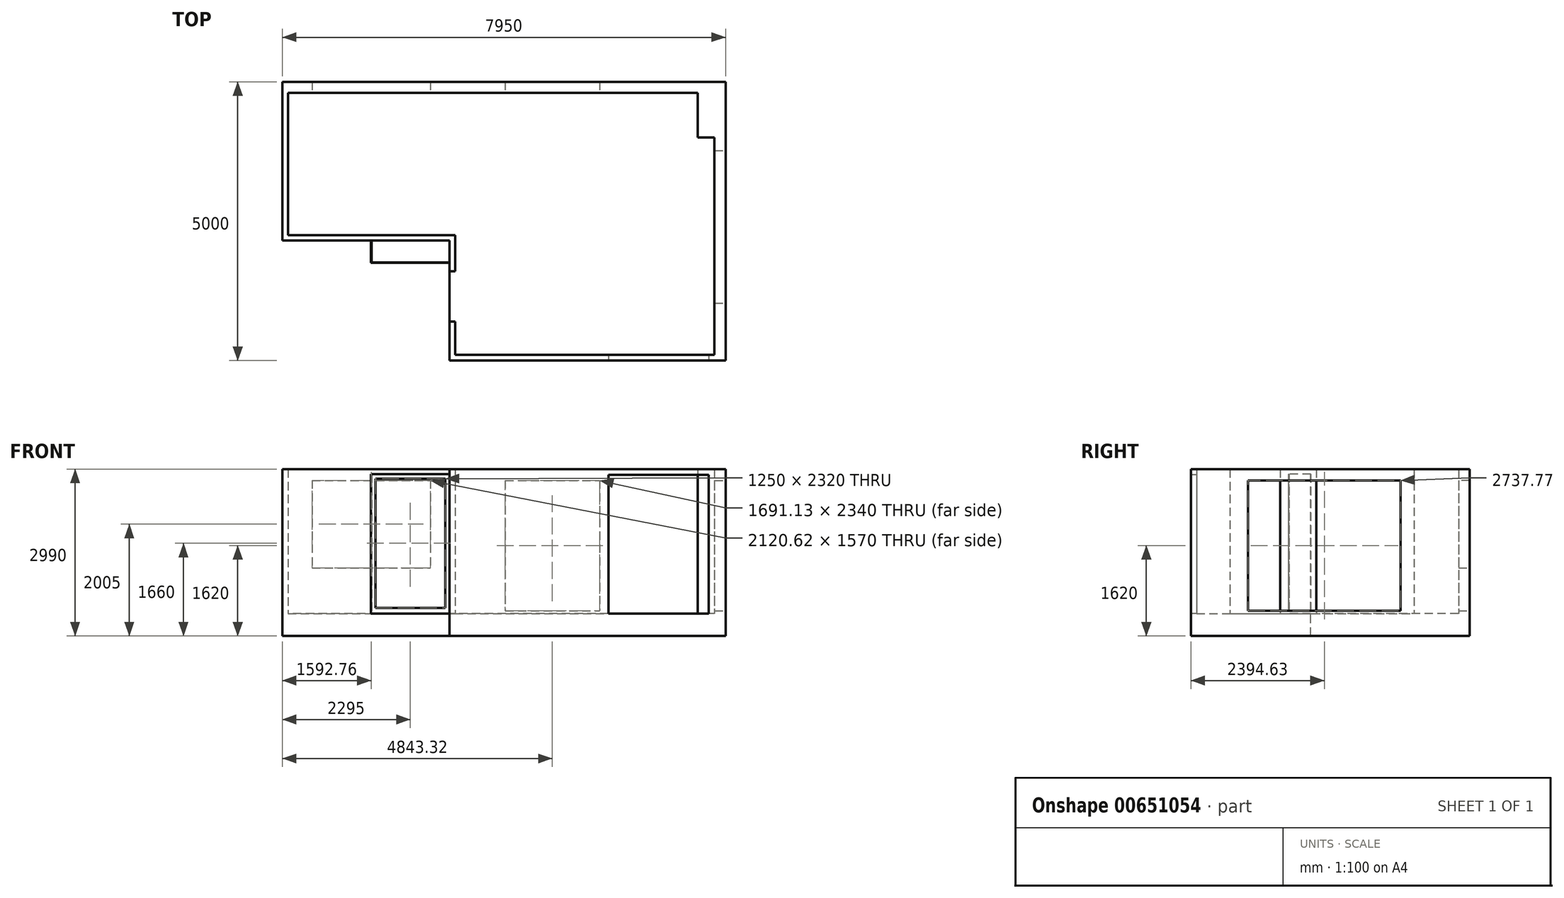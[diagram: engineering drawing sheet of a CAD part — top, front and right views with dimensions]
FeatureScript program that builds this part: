
annotation { "Feature Type Name" : "Feature", "Feature Type Description" : "" }
export const myFeature = defineFeature(function(context is Context, id is Id, definition is map)
    precondition{}
    {
        {
            var Q0;
            Q0=qCreatedBy(makeId("Top.planeOp"),FACE);
            var sketch = newSketch(context, id + "F0", { "sketchPlane" : qUnion([Q0])});
            skLineSegment(sketch, "E0.bottom", {"start": v(0, 0) * mm, "end": v(-4650, 0) * mm});
            skLineSegment(sketch, "E0.left", {"start": v(0, 0) * mm, "end": v(0, 3900) * mm});
            skLineSegment(sketch, "E0.right", {"start": v(-4650, 0) * mm, "end": v(-4650, 2150) * mm});
            skLineSegment(sketch, "E1.top", {"start": v(-4650, 2150) * mm, "end": v(-7650, 2150) * mm});
            skLineSegment(sketch, "E1.right", {"start": v(-7650, 4700) * mm, "end": v(-7650, 2150) * mm});
            skLineSegment(sketch, "E2", {"start": v(-7650, 4700) * mm, "end": v(-300, 4700) * mm});
            skLineSegment(sketch, "E3.bottom", {"start": v(-7750, 4900) * mm, "end": v(200, 4900) * mm});
            skLineSegment(sketch, "E3.top", {"start": v(-4750, -100) * mm, "end": v(200, -100) * mm});
            skLineSegment(sketch, "E3.left", {"start": v(-7750, 4900) * mm, "end": v(-7750, 2050) * mm});
            skLineSegment(sketch, "E3.right", {"start": v(200, 4900) * mm, "end": v(200, -100) * mm});
            skLineSegment(sketch, "E4.top", {"start": v(-7750, 2050) * mm, "end": v(-4750, 2050) * mm});
            skLineSegment(sketch, "E4.right", {"start": v(-4750, -100) * mm, "end": v(-4750, 2050) * mm});
            skLineSegment(sketch, "E5.bottom", {"start": v(-1900, 0) * mm, "end": v(-100, 0) * mm});
            skLineSegment(sketch, "E5.top", {"start": v(-1900, -100) * mm, "end": v(-100, -100) * mm});
            skLineSegment(sketch, "E5.left", {"start": v(-1900, 0) * mm, "end": v(-1900, -100) * mm});
            skLineSegment(sketch, "E5.right", {"start": v(-100, 0) * mm, "end": v(-100, -100) * mm});
            skLineSegment(sketch, "E6.bottom", {"start": v(-4750, 1500) * mm, "end": v(-4650, 1500) * mm});
            skLineSegment(sketch, "E6.top", {"start": v(-4750, 600) * mm, "end": v(-4650, 600) * mm});
            skLineSegment(sketch, "E6.left", {"start": v(-4750, 1500) * mm, "end": v(-4750, 600) * mm});
            skLineSegment(sketch, "E6.right", {"start": v(-4650, 1500) * mm, "end": v(-4650, 600) * mm});
            skLineSegment(sketch, "E7.bottom", {"start": v(-6160, 2050) * mm, "end": v(-4750, 2050) * mm});
            skLineSegment(sketch, "E7.top", {"start": v(-6160, 1650) * mm, "end": v(-4750, 1650) * mm});
            skLineSegment(sketch, "E7.left", {"start": v(-6160, 2050) * mm, "end": v(-6160, 1650) * mm});
            skLineSegment(sketch, "E7.right", {"start": v(-4750, 2050) * mm, "end": v(-4750, 1650) * mm});
            skLineSegment(sketch, "E8.bottom", {"start": v(-6150, 2050) * mm, "end": v(-4750, 2050) * mm});
            skLineSegment(sketch, "E8.top", {"start": v(-6150, 1660) * mm, "end": v(-4750, 1660) * mm});
            skLineSegment(sketch, "E8.left", {"start": v(-6150, 2050) * mm, "end": v(-6150, 1660) * mm});
            skLineSegment(sketch, "E8.right", {"start": v(-4750, 2050) * mm, "end": v(-4750, 1660) * mm});
            skLineSegment(sketch, "E9.top", {"start": v(-300, 3900) * mm, "end": v(0, 3900) * mm});
            skLineSegment(sketch, "E9.left", {"start": v(-300, 4700) * mm, "end": v(-300, 3900) * mm});
            skPoint(sketch, "E10.orphan", {"position": v(0, 4700) * mm});
            skLineSegment(sketch, "E11.bottom", {"start": v(0, 3663.51) * mm, "end": v(200, 3663.51) * mm});
            skLineSegment(sketch, "E11.top", {"start": v(0, 925.75) * mm, "end": v(200, 925.75) * mm});
            skLineSegment(sketch, "E11.left", {"start": v(0, 3663.51) * mm, "end": v(0, 925.75) * mm});
            skLineSegment(sketch, "E11.right", {"start": v(200, 3663.51) * mm, "end": v(200, 925.75) * mm});
            skLineSegment(sketch, "E12.bottom", {"start": v(-3752.24, 4700) * mm, "end": v(-2061.12, 4700) * mm});
            skLineSegment(sketch, "E12.top", {"start": v(-3752.24, 4900) * mm, "end": v(-2061.12, 4900) * mm});
            skLineSegment(sketch, "E12.left", {"start": v(-3752.24, 4700) * mm, "end": v(-3752.24, 4900) * mm});
            skLineSegment(sketch, "E12.right", {"start": v(-2061.12, 4700) * mm, "end": v(-2061.12, 4900) * mm});
            skLineSegment(sketch, "E13.bottom", {"start": v(-7217.55, 4700) * mm, "end": v(-5096.93, 4700) * mm});
            skLineSegment(sketch, "E13.top", {"start": v(-7217.55, 4900) * mm, "end": v(-5096.93, 4900) * mm});
            skLineSegment(sketch, "E13.left", {"start": v(-7217.55, 4700) * mm, "end": v(-7217.55, 4900) * mm});
            skLineSegment(sketch, "E13.right", {"start": v(-5096.93, 4700) * mm, "end": v(-5096.93, 4900) * mm});
            skSolve(sketch);
        }
        {
            var Q0;
            {var subQ7=sQuery(id+"F0.wireOp",EDGE,"E1.top");Q0=makeQuery(id+"F0.imprint","IMPRINT",FACE,{"disambiguationData":[TD([[makeQuery(id+"F0.imprint","IMPRINT",EDGE,{"derivedFrom":subQ7}),1.0]])]});}
            var Q1;
            {var subQ0=sQuery(id+"F0.wireOp",EDGE,"E1.top");Q1=makeQuery(id+"F0.imprint","IMPRINT",FACE,{"disambiguationData":[TD([[makeQuery(id+"F0.imprint","IMPRINT",EDGE,{"derivedFrom":subQ0}),-1.0]])]});}
            var Q2;
            {var subQ2=sQuery(id+"F0.wireOp",EDGE,"E6.bottom");Q2=makeQuery(id+"F0.imprint","IMPRINT",FACE,{"disambiguationData":[TD([[makeQuery(id+"F0.imprint","IMPRINT",EDGE,{"derivedFrom":subQ2}),-1.0]])]});}
            var Q3;
            {var subQ4=sQuery(id+"F0.wireOp",EDGE,"E5.left");Q3=makeQuery(id+"F0.imprint","IMPRINT",FACE,{"disambiguationData":[TD([[makeQuery(id+"F0.imprint","IMPRINT",EDGE,{"derivedFrom":subQ4}),-1.0]])]});}
            var Q4;
            {var subQ0=sQuery(id+"F0.wireOp",EDGE,"E12.left");Q4=makeQuery(id+"F0.imprint","IMPRINT",FACE,{"disambiguationData":[TD([[makeQuery(id+"F0.imprint","IMPRINT",EDGE,{"derivedFrom":subQ0}),-1.0]])]});}
            var Q5;
            {var subQ5=sQuery(id+"F0.wireOp",EDGE,"E9.top");Q5=makeQuery(id+"F0.imprint","IMPRINT",FACE,{"disambiguationData":[TD([[makeQuery(id+"F0.imprint","IMPRINT",EDGE,{"derivedFrom":subQ5}),1.0]])]});}
            var Q6;
            {var subQ0=sQuery(id+"F0.wireOp",EDGE,"E13.left");Q6=makeQuery(id+"F0.imprint","IMPRINT",FACE,{"disambiguationData":[TD([[makeQuery(id+"F0.imprint","IMPRINT",EDGE,{"derivedFrom":subQ0}),-1.0]])]});}
            var Q7;
            {var subQ0=sQuery(id+"F0.wireOp",EDGE,"E12.left");Q7=makeQuery(id+"F0.imprint","IMPRINT",FACE,{"disambiguationData":[TD([[makeQuery(id+"F0.imprint","IMPRINT",EDGE,{"derivedFrom":subQ0}),1.0]])]});}
            var Q8;
            {var subQ2=sQuery(id+"F0.wireOp",EDGE,"E11.bottom");Q8=makeQuery(id+"F0.imprint","IMPRINT",FACE,{"disambiguationData":[TD([[makeQuery(id+"F0.imprint","IMPRINT",EDGE,{"derivedFrom":subQ2}),-1.0]])]});}
            var Q9;
            {var subQ3=sQuery(id+"F0.wireOp",EDGE,"E5.right");Q9=makeQuery(id+"F0.imprint","IMPRINT",FACE,{"disambiguationData":[TD([[makeQuery(id+"F0.imprint","IMPRINT",EDGE,{"derivedFrom":subQ3}),1.0]])]});}
            var Q10;
            {var subQ0=sQuery(id+"F0.wireOp",EDGE,"E5.left");Q10=makeQuery(id+"F0.imprint","IMPRINT",FACE,{"disambiguationData":[TD([[makeQuery(id+"F0.imprint","IMPRINT",EDGE,{"derivedFrom":subQ0}),1.0]])]});}
            extrude(context, id + "F1", {"entities" : qUnion([Q0, Q1, Q2, Q3, Q4, Q5, Q6, Q7, Q8, Q9, Q10]), "oppositeDirection" : true, "depth" : 400 * mm, "offsetDistance" : 25 * mm});
        }
        {
            var Q0;
            {var subQ7=sQuery(id+"F0.wireOp",EDGE,"E1.top");Q0=makeQuery(id+"F0.imprint","IMPRINT",FACE,{"disambiguationData":[TD([[makeQuery(id+"F0.imprint","IMPRINT",EDGE,{"derivedFrom":subQ7}),1.0]])]});}
            var Q1;
            {var subQ0=sQuery(id+"F0.wireOp",EDGE,"E12.left");Q1=makeQuery(id+"F0.imprint","IMPRINT",FACE,{"disambiguationData":[TD([[makeQuery(id+"F0.imprint","IMPRINT",EDGE,{"derivedFrom":subQ0}),1.0]])]});}
            var Q2;
            {var subQ5=sQuery(id+"F0.wireOp",EDGE,"E9.top");Q2=makeQuery(id+"F0.imprint","IMPRINT",FACE,{"disambiguationData":[TD([[makeQuery(id+"F0.imprint","IMPRINT",EDGE,{"derivedFrom":subQ5}),1.0]])]});}
            var Q3;
            {var subQ3=sQuery(id+"F0.wireOp",EDGE,"E5.right");Q3=makeQuery(id+"F0.imprint","IMPRINT",FACE,{"disambiguationData":[TD([[makeQuery(id+"F0.imprint","IMPRINT",EDGE,{"derivedFrom":subQ3}),1.0]])]});}
            var Q4;
            {var subQ4=sQuery(id+"F0.wireOp",EDGE,"E5.left");Q4=makeQuery(id+"F0.imprint","IMPRINT",FACE,{"disambiguationData":[TD([[makeQuery(id+"F0.imprint","IMPRINT",EDGE,{"derivedFrom":subQ4}),-1.0]])]});}
            extrude(context, id + "F2", {"entities" : qUnion([Q0, Q1, Q2, Q3, Q4]), "operationType" : NewBodyOperationType.ADD, "depth" : 2590 * mm, "offsetDistance" : 25 * mm});
        }
        {
            var Q0;
            {var subQ0=sQuery(id+"F0.wireOp",EDGE,"E12.left");Q0=makeQuery(id+"F0.imprint","IMPRINT",FACE,{"disambiguationData":[TD([[makeQuery(id+"F0.imprint","IMPRINT",EDGE,{"derivedFrom":subQ0}),-1.0]])]});}
            var Q1;
            {var subQ2=sQuery(id+"F0.wireOp",EDGE,"E11.bottom");Q1=makeQuery(id+"F0.imprint","IMPRINT",FACE,{"disambiguationData":[TD([[makeQuery(id+"F0.imprint","IMPRINT",EDGE,{"derivedFrom":subQ2}),-1.0]])]});}
            extrude(context, id + "F3", {"entities" : qUnion([Q0, Q1]), "operationType" : NewBodyOperationType.ADD, "depth" : 50 * mm, "offsetDistance" : 25 * mm});
        }
        {
            var Q0;
            {var subQ0=sQuery(id+"F0.wireOp",EDGE,"E13.left");Q0=makeQuery(id+"F0.imprint","IMPRINT",FACE,{"disambiguationData":[TD([[makeQuery(id+"F0.imprint","IMPRINT",EDGE,{"derivedFrom":subQ0}),-1.0]])]});}
            extrude(context, id + "F4", {"entities" : qUnion([Q0]), "operationType" : NewBodyOperationType.ADD, "depth" : 820 * mm, "offsetDistance" : 25 * mm});
        }
        {
            var Q0;
            {var subQ3=sQuery(id+"F0.wireOp",EDGE,"E7.top");Q0=makeQuery(id+"F0.imprint","IMPRINT",FACE,{"disambiguationData":[TD([[makeQuery(id+"F0.imprint","IMPRINT",EDGE,{"derivedFrom":subQ3}),1.0]])]});}
            extrude(context, id + "F5", {"entities" : qUnion([Q0]), "operationType" : NewBodyOperationType.ADD, "depth" : 2500 * mm, "offsetDistance" : 25 * mm});
        }
        {
            var Q0;
            Q0=makeQuery(id+"F5.opExtrude","SWEPT_FACE",FACE,{"disambiguationData":[OSD([sQuery(id+"F0.wireOp",EDGE,"E7.top")])]});
            var sketch = newSketch(context, id + "F6", { "sketchPlane" : qUnion([Q0])});
            skLineSegment(sketch, "E14.0.0", {"start": v(-6160, 0) * mm, "end": v(-4750, 0) * mm});
            skLineSegment(sketch, "E14.0.1", {"start": v(-4750, 0) * mm, "end": v(-4750, 2500) * mm});
            skLineSegment(sketch, "E14.0.2", {"start": v(-4750, 2500) * mm, "end": v(-6160, 2500) * mm});
            skLineSegment(sketch, "E14.0.3", {"start": v(-6160, 2500) * mm, "end": v(-6160, 0) * mm});
            skLineSegment(sketch, "E15.bottom", {"start": v(-6080, 2420) * mm, "end": v(-4830, 2420) * mm});
            skLineSegment(sketch, "E15.top", {"start": v(-6080, 100) * mm, "end": v(-4830, 100) * mm});
            skLineSegment(sketch, "E15.left", {"start": v(-6080, 2420) * mm, "end": v(-6080, 100) * mm});
            skLineSegment(sketch, "E15.right", {"start": v(-4830, 2420) * mm, "end": v(-4830, 100) * mm});
            skSolve(sketch);
        }
        {
            var Q0;
            Q0=makeQuery(id+"F6.imprint","IMPRINT",FACE,{"disambiguationData":[TD([[makeQuery(id+"F6.imprint","IMPRINT",EDGE,{"derivedFrom":sQuery(id+"F6.wireOp",EDGE,"E15.bottom")}),-1.0]])]});
            extrude(context, id + "F7", {"entities" : qUnion([Q0]), "operationType" : NewBodyOperationType.REMOVE, "oppositeDirection" : true, "depth" : 25 * mm, "offsetDistance" : 25 * mm});
        }
        {
            var Q0;
            {var subQ0=sQuery(id+"F0.wireOp",EDGE,"E2");Q0=makeQuery(id+"F4.boolean.opBoolean","MERGE",FACE,{"derivedFrom":[makeQuery(id+"F2.opExtrude","SWEPT_FACE",FACE,{"disambiguationData":[OSD([subQ0]),TDD([makeQuery(id+"F0.imprint","IMPRINT",EDGE,{"disambiguationData":[TD([[makeQuery(id+"F0.imprint","INTERSECT",VERTEX,{"derivedFrom":[sQuery(id+"F0.wireOp",EDGE,"E1.right"),subQ0]}),-1.0]])],"derivedFrom":subQ0})])]}),makeQuery(id+"F3.boolean.opBoolean","MERGE",FACE,{"derivedFrom":[makeQuery(id+"F2.opExtrude","SWEPT_FACE",FACE,{"disambiguationData":[OSD([subQ0]),TDD([makeQuery(id+"F0.imprint","IMPRINT",EDGE,{"disambiguationData":[TD([[makeQuery(id+"F0.imprint","INTERSECT",VERTEX,{"derivedFrom":[subQ0,sQuery(id+"F0.wireOp",EDGE,"E9.left")]}),1.0]])],"derivedFrom":subQ0})])]}),makeQuery(id+"F2.opExtrude","SWEPT_FACE",FACE,{"disambiguationData":[OSD([subQ0]),TDD([makeQuery(id+"F0.imprint","IMPRINT",EDGE,{"disambiguationData":[TD([[makeQuery(id+"F0.imprint","INTERSECT",VERTEX,{"derivedFrom":[subQ0,sQuery(id+"F0.wireOp",EDGE,"E12.left")]}),1.0]])],"derivedFrom":subQ0})])]}),makeQuery(id+"F3.opExtrude","SWEPT_FACE",FACE,{"disambiguationData":[OSD([subQ0])]})]}),makeQuery(id+"F4.opExtrude","SWEPT_FACE",FACE,{"disambiguationData":[OSD([subQ0])]})]});}
            var sketch = newSketch(context, id + "F8", { "sketchPlane" : qUnion([Q0])});
            skLineSegment(sketch, "E16.0.0", {"start": v(-7650, 0) * mm, "end": v(-300, 0) * mm});
            skLineSegment(sketch, "E16.0.1", {"start": v(-300, 0) * mm, "end": v(-300, 2590) * mm});
            skLineSegment(sketch, "E16.0.2", {"start": v(-300, 2590) * mm, "end": v(-2061.12, 2590) * mm});
            skLineSegment(sketch, "E16.0.3", {"start": v(-2061.12, 2590) * mm, "end": v(-2061.12, 50) * mm});
            skLineSegment(sketch, "E16.0.4", {"start": v(-2061.12, 50) * mm, "end": v(-3752.24, 50) * mm});
            skLineSegment(sketch, "E16.0.5", {"start": v(-3752.24, 50) * mm, "end": v(-3752.24, 2590) * mm});
            skLineSegment(sketch, "E16.0.6", {"start": v(-3752.24, 2590) * mm, "end": v(-5096.93, 2590) * mm});
            skLineSegment(sketch, "E16.0.7", {"start": v(-5096.93, 2590) * mm, "end": v(-5096.93, 820) * mm});
            skLineSegment(sketch, "E16.0.8", {"start": v(-5096.93, 820) * mm, "end": v(-7217.55, 820) * mm});
            skLineSegment(sketch, "E16.0.9", {"start": v(-7217.55, 820) * mm, "end": v(-7217.55, 2590) * mm});
            skLineSegment(sketch, "E16.0.10", {"start": v(-7217.55, 2590) * mm, "end": v(-7650, 2590) * mm});
            skLineSegment(sketch, "E16.0.11", {"start": v(-7650, 2590) * mm, "end": v(-7650, 0) * mm});
            skLineSegment(sketch, "E17.bottom", {"start": v(-7217.55, 2590) * mm, "end": v(-5096.93, 2590) * mm});
            skLineSegment(sketch, "E17.top", {"start": v(-7217.55, 2390) * mm, "end": v(-5096.93, 2390) * mm});
            skLineSegment(sketch, "E17.left", {"start": v(-7217.55, 2590) * mm, "end": v(-7217.55, 2390) * mm});
            skLineSegment(sketch, "E17.right", {"start": v(-5096.93, 2590) * mm, "end": v(-5096.93, 2390) * mm});
            skLineSegment(sketch, "E18.bottom", {"start": v(-3752.24, 2590) * mm, "end": v(-2061.12, 2590) * mm});
            skLineSegment(sketch, "E18.top", {"start": v(-3752.24, 2390) * mm, "end": v(-2061.12, 2390) * mm});
            skLineSegment(sketch, "E18.left", {"start": v(-3752.24, 2590) * mm, "end": v(-3752.24, 2390) * mm});
            skLineSegment(sketch, "E18.right", {"start": v(-2061.12, 2590) * mm, "end": v(-2061.12, 2390) * mm});
            skSolve(sketch);
        }
        {
            var Q0;
            Q0=makeQuery(id+"F8.imprint","IMPRINT",FACE,{"disambiguationData":[TD([[makeQuery(id+"F8.imprint","IMPRINT",EDGE,{"derivedFrom":sQuery(id+"F8.wireOp",EDGE,"E17.bottom")}),-1.0]])]});
            var Q1;
            Q1=makeQuery(id+"F8.imprint","IMPRINT",FACE,{"disambiguationData":[TD([[makeQuery(id+"F8.imprint","IMPRINT",EDGE,{"derivedFrom":sQuery(id+"F8.wireOp",EDGE,"E18.bottom")}),-1.0]])]});
            extrude(context, id + "F9", {"entities" : qUnion([Q0, Q1]), "operationType" : NewBodyOperationType.ADD, "oppositeDirection" : true, "depth" : 200 * mm, "offsetDistance" : 25 * mm});
        }
        {
            var Q0;
            {var subQ0=sQuery(id+"F0.wireOp",EDGE,"E3.top");Q0=makeQuery(id+"F2.boolean.opBoolean","MERGE",FACE,{"derivedFrom":[makeQuery(id+"F1.opExtrude","SWEPT_FACE",FACE,{"disambiguationData":[OSD([subQ0])]}),makeQuery(id+"F2.opExtrude","SWEPT_FACE",FACE,{"disambiguationData":[OSD([subQ0]),TDD([makeQuery(id+"F0.imprint","IMPRINT",EDGE,{"disambiguationData":[TD([[makeQuery(id+"F0.imprint","INTERSECT",VERTEX,{"derivedFrom":[subQ0,sQuery(id+"F0.wireOp",EDGE,"E4.right")]}),-1.0]])],"derivedFrom":subQ0})])]}),makeQuery(id+"F2.opExtrude","SWEPT_FACE",FACE,{"disambiguationData":[OSD([subQ0]),TDD([makeQuery(id+"F0.imprint","IMPRINT",EDGE,{"disambiguationData":[TD([[makeQuery(id+"F0.imprint","INTERSECT",VERTEX,{"derivedFrom":[subQ0,sQuery(id+"F0.wireOp",EDGE,"E3.right")]}),1.0]])],"derivedFrom":subQ0})])]})]});}
            var sketch = newSketch(context, id + "F10", { "sketchPlane" : qUnion([Q0])});
            skLineSegment(sketch, "E19.bottom", {"start": v(-1900, 2590) * mm, "end": v(-100, 2590) * mm});
            skLineSegment(sketch, "E19.top", {"start": v(-1900, 2490) * mm, "end": v(-100, 2490) * mm});
            skLineSegment(sketch, "E19.left", {"start": v(-1900, 2590) * mm, "end": v(-1900, 2490) * mm});
            skLineSegment(sketch, "E19.right", {"start": v(-100, 2590) * mm, "end": v(-100, 2490) * mm});
            skSolve(sketch);
        }
        {
            var Q0;
            Q0=qSketchRegion(id+"F10",true);
            extrude(context, id + "F11", {"entities" : qUnion([Q0]), "operationType" : NewBodyOperationType.ADD, "oppositeDirection" : true, "depth" : 100 * mm, "offsetDistance" : 25 * mm});
        }
        {
            var Q0;
            {var subQ0=sQuery(id+"F0.wireOp",EDGE,"E3.right");Q0=makeQuery(id+"F3.boolean.opBoolean","MERGE",FACE,{"derivedFrom":[makeQuery(id+"F2.boolean.opBoolean","MERGE",FACE,{"derivedFrom":[makeQuery(id+"F1.opExtrude","SWEPT_FACE",FACE,{"disambiguationData":[OSD([subQ0])]}),makeQuery(id+"F2.opExtrude","SWEPT_FACE",FACE,{"disambiguationData":[OSD([subQ0]),TDD([makeQuery(id+"F0.imprint","IMPRINT",EDGE,{"disambiguationData":[TD([[makeQuery(id+"F0.imprint","INTERSECT",VERTEX,{"derivedFrom":[subQ0,sQuery(id+"F0.wireOp",EDGE,"E11.bottom")]}),1.0]])],"derivedFrom":subQ0})])]}),makeQuery(id+"F2.opExtrude","SWEPT_FACE",FACE,{"disambiguationData":[OSD([subQ0]),TDD([makeQuery(id+"F0.imprint","IMPRINT",EDGE,{"disambiguationData":[TD([[makeQuery(id+"F0.imprint","INTERSECT",VERTEX,{"derivedFrom":[sQuery(id+"F0.wireOp",EDGE,"E3.top"),subQ0]}),1.0]])],"derivedFrom":subQ0})])]})]}),makeQuery(id+"F3.opExtrude","SWEPT_FACE",FACE,{"disambiguationData":[OSD([subQ0])]})]});}
            var sketch = newSketch(context, id + "F12", { "sketchPlane" : qUnion([Q0])});
            skLineSegment(sketch, "E20.0.0", {"start": v(4900, -400) * mm, "end": v(4900, 2590) * mm});
            skLineSegment(sketch, "E20.0.1", {"start": v(4900, 2590) * mm, "end": v(3663.51, 2590) * mm});
            skLineSegment(sketch, "E20.0.2", {"start": v(3663.51, 2590) * mm, "end": v(3663.51, 50) * mm});
            skLineSegment(sketch, "E20.0.3", {"start": v(3663.51, 50) * mm, "end": v(925.75, 50) * mm});
            skLineSegment(sketch, "E20.0.4", {"start": v(925.75, 50) * mm, "end": v(925.75, 2590) * mm});
            skLineSegment(sketch, "E20.0.5", {"start": v(925.75, 2590) * mm, "end": v(-100, 2590) * mm});
            skLineSegment(sketch, "E20.0.6", {"start": v(-100, 2590) * mm, "end": v(-100, -400) * mm});
            skLineSegment(sketch, "E20.0.7", {"start": v(-100, -400) * mm, "end": v(4900, -400) * mm});
            skLineSegment(sketch, "E21.bottom", {"start": v(925.75, 2590) * mm, "end": v(3663.51, 2590) * mm});
            skLineSegment(sketch, "E21.top", {"start": v(925.75, 2390) * mm, "end": v(3663.51, 2390) * mm});
            skLineSegment(sketch, "E21.left", {"start": v(925.75, 2590) * mm, "end": v(925.75, 2390) * mm});
            skLineSegment(sketch, "E21.right", {"start": v(3663.51, 2590) * mm, "end": v(3663.51, 2390) * mm});
            skSolve(sketch);
        }
        {
            var Q0;
            Q0=qSketchRegion(id+"F12",true);
            extrude(context, id + "F13", {"entities" : qUnion([Q0]), "operationType" : NewBodyOperationType.ADD, "oppositeDirection" : true, "depth" : 200 * mm, "offsetDistance" : 25 * mm});
        }
    });
